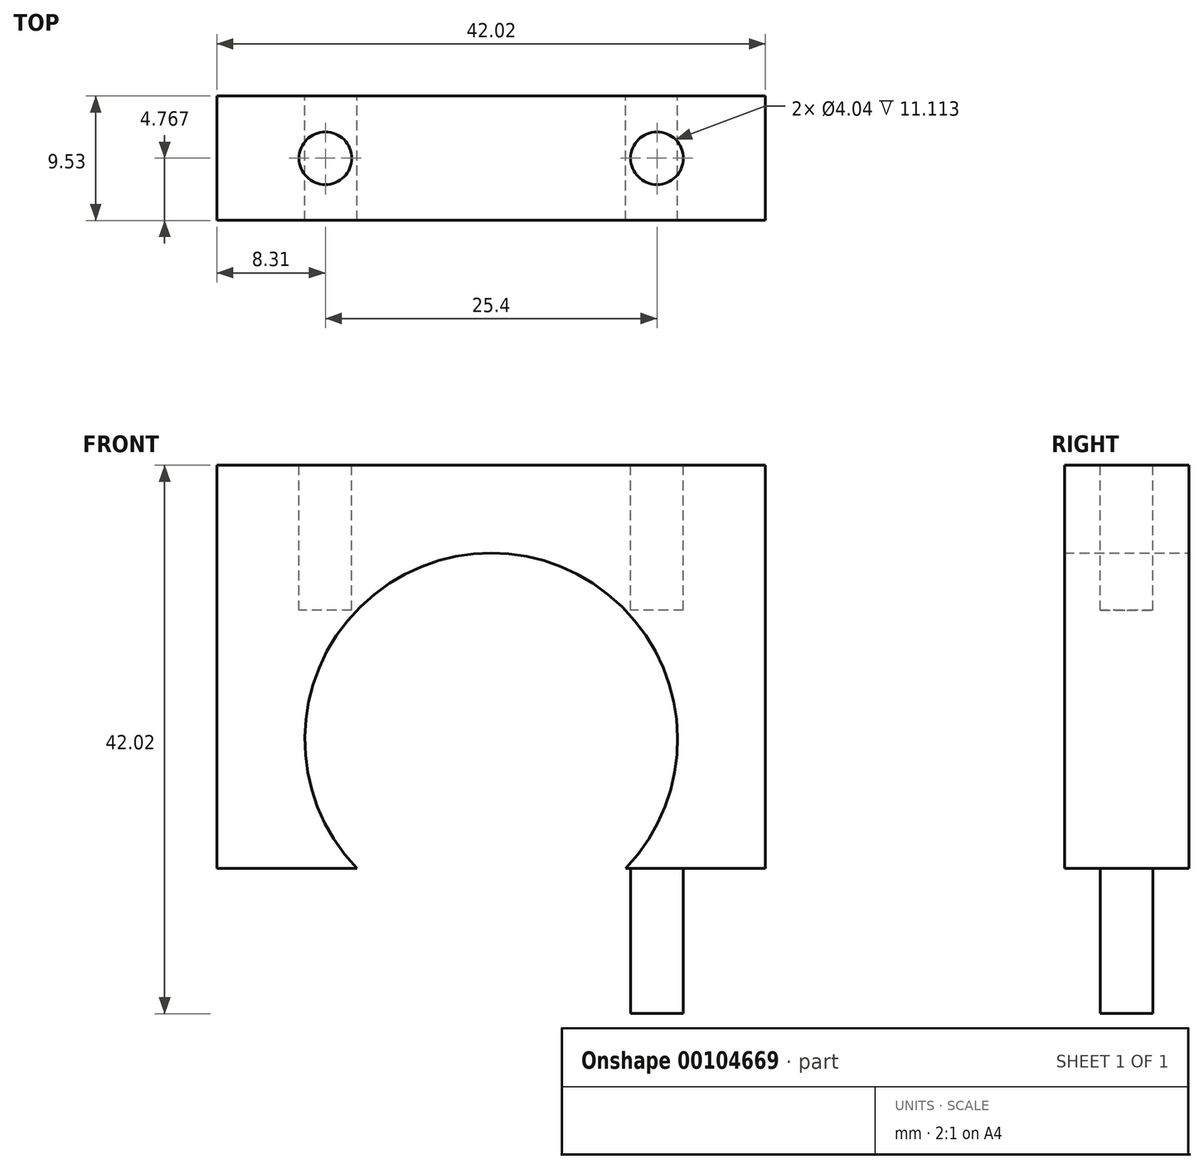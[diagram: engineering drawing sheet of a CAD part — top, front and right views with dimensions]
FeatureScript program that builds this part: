
annotation { "Feature Type Name" : "Feature", "Feature Type Description" : "" }
export const myFeature = defineFeature(function(context is Context, id is Id, definition is map)
    precondition{}
    {
        {
            var Q0;
            Q0=qCreatedBy(makeId("Front.planeOp"),FACE);
            var sketch = newSketch(context, id + "F0", { "sketchPlane" : qUnion([Q0])});
            skLineSegment(sketch, "E0.bottom", {"start": v(21, -21) * mm, "end": v(-21, -21) * mm});
            skLineSegment(sketch, "E0.top", {"start": v(21, 21) * mm, "end": v(-21, 21) * mm});
            skLineSegment(sketch, "E0.left", {"start": v(21, -21) * mm, "end": v(21, 21) * mm});
            skLineSegment(sketch, "E0.right", {"start": v(-21, -21) * mm, "end": v(-21, 21) * mm});
            skPoint(sketch, "E0.middle", {"position": v(0, 0) * mm});
            skCircle(sketch, "E1", {"center": v(0, 0) * mm, "radius": 14.27 * mm});
            skSolve(sketch);
        }
        {
            var Q0;
            Q0=makeQuery(id+"F0.imprint","IMPRINT",FACE,{"disambiguationData":[TD([[makeQuery(id+"F0.imprint","IMPRINT",EDGE,{"derivedFrom":sQuery(id+"F0.wireOp",EDGE,"E0.bottom")}),-1.0]])]});
            extrude(context, id + "F1", {"entities" : qUnion([Q0]), "depth" : 9.52 * mm});
        }
        {
            var Q0;
            Q0=makeQuery(id+"F1.opExtrude","SWEPT_FACE",FACE,{"disambiguationData":[OSD([sQuery(id+"F0.wireOp",EDGE,"E0.top")])]});
            var sketch = newSketch(context, id + "F2", { "sketchPlane" : qUnion([Q0])});
            skCircle(sketch, "E2", {"center": v(-12.7, -4.76) * mm, "radius": 2.02 * mm});
            skCircle(sketch, "E3", {"center": v(12.7, -4.76) * mm, "radius": 2.02 * mm});
            skSolve(sketch);
        }
        {
            var Q0;
            Q0=makeQuery(id+"F2.imprint","IMPRINT",FACE,{"disambiguationData":[TD([[makeQuery(id+"F2.imprint","IMPRINT",EDGE,{"derivedFrom":sQuery(id+"F2.wireOp",EDGE,"E2")}),1.0]])]});
            var Q1;
            Q1=makeQuery(id+"F2.imprint","IMPRINT",FACE,{"disambiguationData":[TD([[makeQuery(id+"F2.imprint","IMPRINT",EDGE,{"derivedFrom":sQuery(id+"F2.wireOp",EDGE,"E3")}),1.0]])]});
            extrude(context, id + "F3", {"entities" : qUnion([Q0, Q1]), "operationType" : NewBodyOperationType.REMOVE, "oppositeDirection" : true, "depth" : 11.1 * mm});
        }
        {
            var Q0;
            Q0=makeQuery(id+"F1.opExtrude","SWEPT_FACE",FACE,{"disambiguationData":[OSD([sQuery(id+"F0.wireOp",EDGE,"E0.bottom")])]});
            var sketch = newSketch(context, id + "F4", { "sketchPlane" : qUnion([Q0])});
            skCircle(sketch, "E4", {"center": v(-12.7, 4.76) * mm, "radius": 2.02 * mm});
            skCircle(sketch, "E5.MirrorC", {"center": v(12.7, 4.76) * mm, "radius": 2.02 * mm});
            skSolve(sketch);
        }
        {
            var Q0;
            Q0=makeQuery(id+"F4.imprint","IMPRINT",FACE,{"disambiguationData":[TD([[makeQuery(id+"F4.imprint","IMPRINT",EDGE,{"derivedFrom":sQuery(id+"F4.wireOp",EDGE,"E4")}),1.0]])]});
            var Q1;
            Q1=makeQuery(id+"F4.imprint","IMPRINT",FACE,{"disambiguationData":[TD([[makeQuery(id+"F4.imprint","IMPRINT",EDGE,{"derivedFrom":sQuery(id+"F4.wireOp",EDGE,"E5.MirrorC")}),-1.0]])]});
            extrude(context, id + "F5", {"entities" : qUnion([Q0, Q1]), "operationType" : NewBodyOperationType.REMOVE, "oppositeDirection" : true, "depth" : 11.1 * mm});
        }
    });
